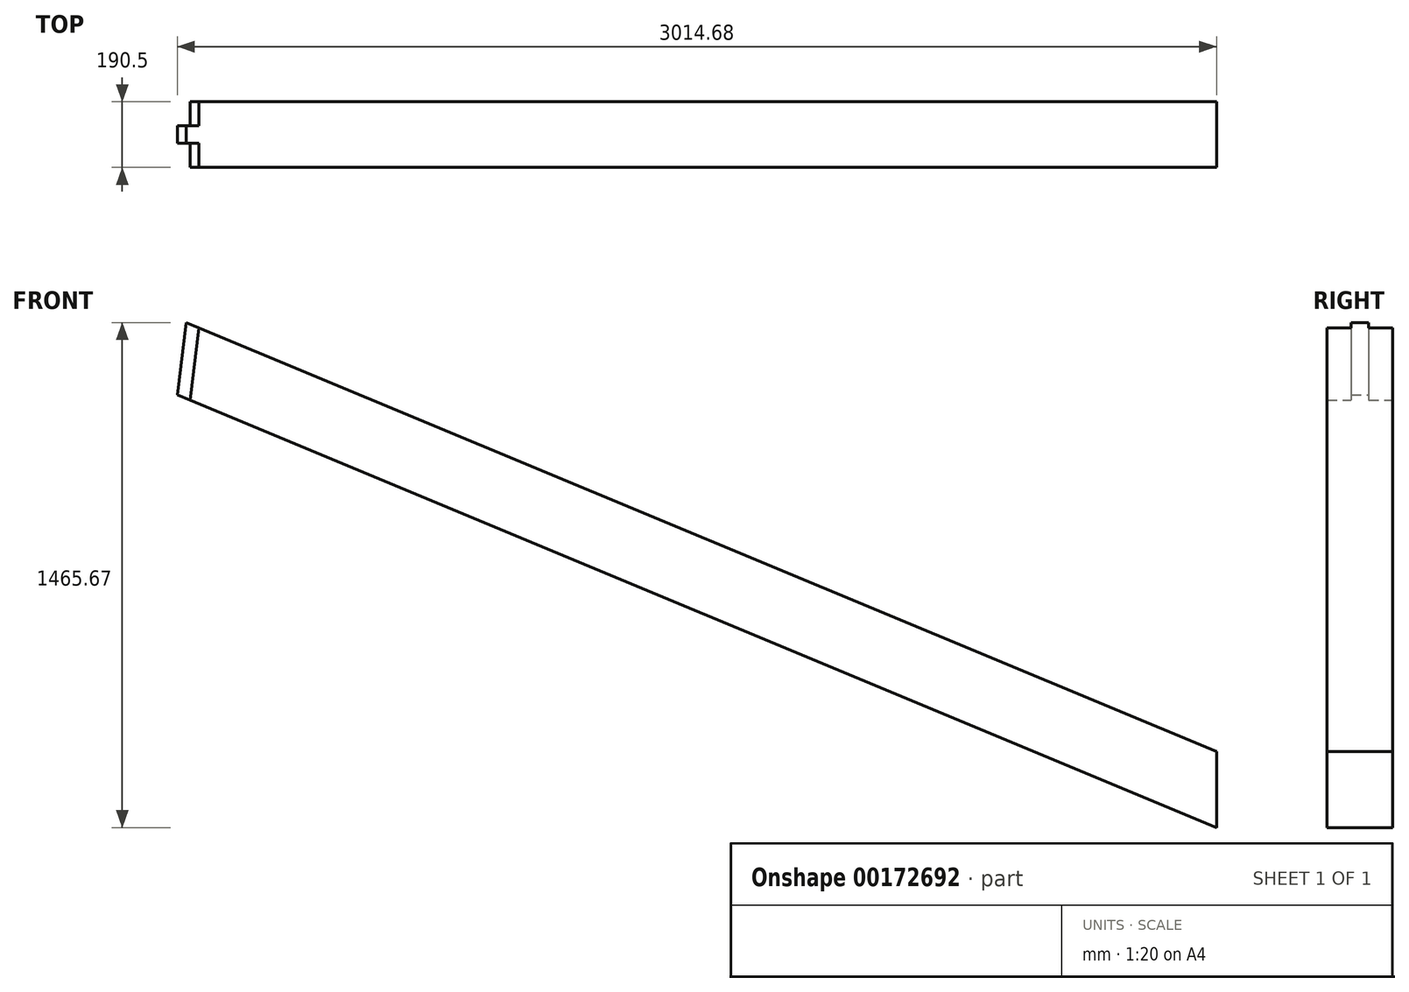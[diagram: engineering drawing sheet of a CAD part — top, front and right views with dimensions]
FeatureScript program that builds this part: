
annotation { "Feature Type Name" : "Feature", "Feature Type Description" : "" }
export const myFeature = defineFeature(function(context is Context, id is Id, definition is map)
    precondition{}
    {
        {
            var Q0;
            Q0=qCreatedBy(makeId("Front.planeOp"),FACE);
            var sketch = newSketch(context, id + "F0", { "sketchPlane" : qUnion([Q0])});
            skLineSegment(sketch, "E0.bottom", {"start": v(-95.25, 1092.85) * mm, "end": v(95.25, 1092.85) * mm});
            skLineSegment(sketch, "E0.top", {"start": v(-95.25, -101.6) * mm, "end": v(95.25, -101.6) * mm});
            skLineSegment(sketch, "E0.left", {"start": v(-95.25, 833.03) * mm, "end": v(-95.25, 203.2) * mm});
            skLineSegment(sketch, "E0.right", {"start": v(95.25, 833.03) * mm, "end": v(95.25, 203.2) * mm});
            skLineSegment(sketch, "E1", {"start": v(-95.25, 0) * mm, "end": v(95.25, 0) * mm});
            skLineSegment(sketch, "E2", {"start": v(95.25, 0) * mm, "end": v(2094.52, 0) * mm});
            skLineSegment(sketch, "E3", {"start": v(2094.52, 0) * mm, "end": v(1606.84, 203.2) * mm});
            skLineSegment(sketch, "E4", {"start": v(1606.84, 203.2) * mm, "end": v(95.25, 203.2) * mm});
            skLineSegment(sketch, "E5", {"start": v(95.25, 203.2) * mm, "end": v(-95.25, 203.2) * mm});
            skLineSegment(sketch, "E6", {"start": v(-95.25, 203.2) * mm, "end": v(-1606.84, 203.2) * mm});
            skLineSegment(sketch, "E7", {"start": v(-1606.84, 203.2) * mm, "end": v(-2094.52, 0) * mm});
            skLineSegment(sketch, "E8", {"start": v(-2094.52, 0) * mm, "end": v(-95.25, 0) * mm});
            skLineSegment(sketch, "E9", {"start": v(1850.68, 101.6) * mm, "end": v(1820.2, 101.6) * mm});
            skLineSegment(sketch, "E10", {"start": v(1820.2, 101.6) * mm, "end": v(1820.2, 114.3) * mm});
            skLineSegment(sketch, "E11", {"start": v(1606.84, 203.2) * mm, "end": v(95.25, 833.03) * mm});
            skLineSegment(sketch, "E12", {"start": v(33.32, 858.84) * mm, "end": v(0, 872.72) * mm});
            skLineSegment(sketch, "E13", {"start": v(0, 872.72) * mm, "end": v(0, 1092.85) * mm});
            skLineSegment(sketch, "E14", {"start": v(0, 1092.85) * mm, "end": v(69.85, 1063.75) * mm});
            skLineSegment(sketch, "E15", {"start": v(95.25, 1053.16) * mm, "end": v(3048, -177.15) * mm});
            skLineSegment(sketch, "E16", {"start": v(3048, -177.15) * mm, "end": v(3048, -397.28) * mm});
            skLineSegment(sketch, "E17", {"start": v(3048, -397.28) * mm, "end": v(2094.52, 0) * mm});
            skLineSegment(sketch, "E18", {"start": v(1014.13, 450.16) * mm, "end": v(1092.29, 637.73) * mm});
            skLineSegment(sketch, "E19", {"start": v(2235.2, -58.62) * mm, "end": v(2235.2, -2361.55) * mm});
            skLineSegment(sketch, "E20", {"start": v(2235.2, -2361.55) * mm, "end": v(2438.4, -2361.55) * mm});
            skLineSegment(sketch, "E21", {"start": v(2438.4, -2361.55) * mm, "end": v(2438.4, -143.28) * mm});
            skLineSegment(sketch, "E22", {"start": v(0, 0) * mm, "end": v(0, -1827.58) * mm});
            skLineSegment(sketch, "E23", {"start": v(2438.4, -143.28) * mm, "end": v(2438.4, 76.85) * mm});
            skLineSegment(sketch, "E24", {"start": v(69.85, 1063.75) * mm, "end": v(69.85, 843.61) * mm});
            skLineSegment(sketch, "E25", {"start": v(95.25, 1053.16) * mm, "end": v(69.85, 843.61) * mm});
            skLineSegment(sketch, "E26.0", {"start": v(58.72, 1068.39) * mm, "end": v(33.32, 858.84) * mm});
            skLineSegment(sketch, "E27.MirrorCS", {"start": v(0, 1092.85) * mm, "end": v(-69.85, 1063.75) * mm});
            skLineSegment(sketch, "E28.MirrorCS", {"start": v(-33.32, 858.84) * mm, "end": v(0, 872.72) * mm});
            skLineSegment(sketch, "E29.MirrorCS", {"start": v(-95.25, 1053.16) * mm, "end": v(-69.85, 843.61) * mm});
            skLineSegment(sketch, "E30.MirrorCS", {"start": v(-1014.13, 450.16) * mm, "end": v(-1092.29, 637.73) * mm});
            skLineSegment(sketch, "E31.MirrorCS", {"start": v(-69.85, 1063.75) * mm, "end": v(-69.85, 843.61) * mm});
            skLineSegment(sketch, "E32.MirrorCS", {"start": v(-58.72, 1068.39) * mm, "end": v(-33.32, 858.84) * mm});
            skLineSegment(sketch, "E33.MirrorCS", {"start": v(-95.25, 1053.16) * mm, "end": v(-3048, -177.15) * mm});
            skLineSegment(sketch, "E34.MirrorCS", {"start": v(-1606.84, 203.2) * mm, "end": v(-95.25, 833.03) * mm});
            skLineSegment(sketch, "E35.MirrorCS", {"start": v(-3048, -177.15) * mm, "end": v(-3048, -397.28) * mm});
            skLineSegment(sketch, "E36.MirrorCS", {"start": v(-3048, -397.28) * mm, "end": v(-2094.52, 0) * mm});
            skLineSegment(sketch, "E37.MirrorCS", {"start": v(-2235.2, -58.62) * mm, "end": v(-2235.2, -2361.55) * mm});
            skLineSegment(sketch, "E38.MirrorCS", {"start": v(-2235.2, -2361.55) * mm, "end": v(-2438.4, -2361.55) * mm});
            skLineSegment(sketch, "E39.MirrorCS", {"start": v(-2438.4, -2361.55) * mm, "end": v(-2438.4, -143.28) * mm});
            skLineSegment(sketch, "E40", {"start": v(95.25, 833.03) * mm, "end": v(95.25, 1053.16) * mm});
            skLineSegment(sketch, "E41", {"start": v(95.25, 1092.85) * mm, "end": v(95.25, 1053.16) * mm});
            skLineSegment(sketch, "E42", {"start": v(-95.25, 833.03) * mm, "end": v(-95.25, 1053.16) * mm});
            skLineSegment(sketch, "E43", {"start": v(-95.25, 1092.85) * mm, "end": v(-95.25, 1053.16) * mm});
            skLineSegment(sketch, "E44", {"start": v(33.32, 858.84) * mm, "end": v(69.85, 843.61) * mm});
            skLineSegment(sketch, "E45", {"start": v(95.25, 833.03) * mm, "end": v(69.85, 843.61) * mm});
            skLineSegment(sketch, "E46", {"start": v(-33.32, 858.84) * mm, "end": v(-69.85, 843.61) * mm});
            skLineSegment(sketch, "E47", {"start": v(-95.25, 833.03) * mm, "end": v(-69.85, 843.61) * mm});
            skLineSegment(sketch, "E48", {"start": v(-95.25, 1053.16) * mm, "end": v(-58.72, 1068.39) * mm});
            skLineSegment(sketch, "E49", {"start": v(58.72, 1068.39) * mm, "end": v(69.85, 1063.75) * mm});
            skLineSegment(sketch, "E50", {"start": v(58.72, 1068.39) * mm, "end": v(95.25, 1053.16) * mm});
            skLineSegment(sketch, "E51", {"start": v(-69.85, 1063.75) * mm, "end": v(-58.72, 1068.39) * mm});
            skLineSegment(sketch, "E52", {"start": v(-95.25, 203.2) * mm, "end": v(-95.25, 0) * mm});
            skLineSegment(sketch, "E53", {"start": v(-95.25, 0) * mm, "end": v(-95.25, -101.6) * mm});
            skLineSegment(sketch, "E54", {"start": v(95.25, 203.2) * mm, "end": v(95.25, 0) * mm});
            skLineSegment(sketch, "E55", {"start": v(95.25, 0) * mm, "end": v(95.25, -101.6) * mm});
            skSolve(sketch);
        }
        {
            var Q0;
            {var subQ2=sQuery(id+"F0.wireOp",EDGE,"E18");Q0=makeQuery(id+"F0.imprint","IMPRINT",FACE,{"disambiguationData":[TD([[makeQuery(id+"F0.imprint","IMPRINT",EDGE,{"derivedFrom":subQ2}),1.0]])]});}
            var Q1;
            Q1=makeQuery(id+"F0.imprint","IMPRINT",FACE,{"disambiguationData":[TD([[makeQuery(id+"F0.imprint","IMPRINT",EDGE,{"derivedFrom":sQuery(id+"F0.wireOp",EDGE,"E25")}),1.0]])]});
            var Q2;
            {var subQ3=sQuery(id+"F0.wireOp",EDGE,"E18");Q2=makeQuery(id+"F0.imprint","IMPRINT",FACE,{"disambiguationData":[TD([[makeQuery(id+"F0.imprint","IMPRINT",EDGE,{"derivedFrom":subQ3}),-1.0]])]});}
            var Q3;
            {var subQ0=sQuery(id+"F0.wireOp",EDGE,"E16");Q3=makeQuery(id+"F0.imprint","IMPRINT",FACE,{"disambiguationData":[TD([[makeQuery(id+"F0.imprint","IMPRINT",EDGE,{"derivedFrom":subQ0}),-1.0]])]});}
            extrude(context, id + "F1", {"entities" : qUnion([Q0, Q1, Q2, Q3]), "endBound" : BoundingType.SYMMETRIC, "depth" : 190.5 * mm});
        }
        {
            var Q0;
            {var subQ0=sQuery(id+"F0.wireOp",EDGE,"E24");Q0=makeQuery(id+"F0.imprint","IMPRINT",FACE,{"disambiguationData":[TD([[makeQuery(id+"F0.imprint","IMPRINT",EDGE,{"derivedFrom":subQ0}),1.0]])]});}
            var Q1;
            {var subQ0=sQuery(id+"F0.wireOp",EDGE,"E24");Q1=makeQuery(id+"F0.imprint","IMPRINT",FACE,{"disambiguationData":[TD([[makeQuery(id+"F0.imprint","IMPRINT",EDGE,{"derivedFrom":subQ0}),-1.0]])]});}
            extrude(context, id + "F2", {"entities" : qUnion([Q0, Q1]), "operationType" : NewBodyOperationType.ADD, "endBound" : BoundingType.SYMMETRIC, "depth" : 50.8 * mm});
        }
    });
